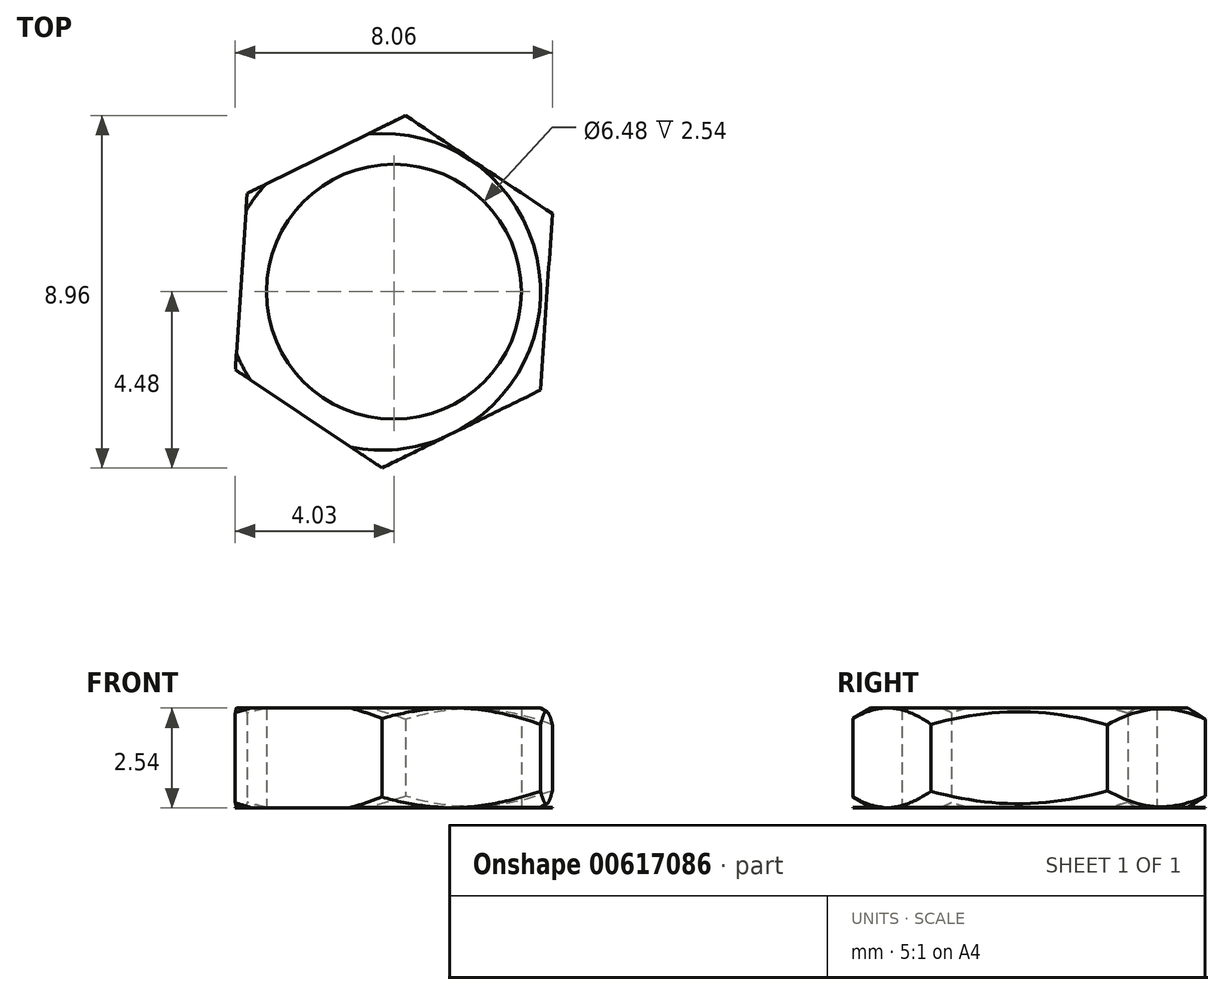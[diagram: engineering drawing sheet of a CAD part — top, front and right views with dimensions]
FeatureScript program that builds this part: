
annotation { "Feature Type Name" : "Feature", "Feature Type Description" : "" }
export const myFeature = defineFeature(function(context is Context, id is Id, definition is map)
    precondition{}
    {
        {
            var Q0;
            Q0=qCreatedBy(makeId("Top.planeOp"),FACE);
            var sketch = newSketch(context, id + "F0", { "sketchPlane" : qUnion([Q0])});
            skCircle(sketch, "E0.cCircle", {"center": v(0, 0) * mm, "radius": 3.89 * mm, "construction": true});
            skLineSegment(sketch, "E0.0", {"start": v(3.73, -2.5) * mm, "end": v(-0.3, -4.48) * mm});
            skLineSegment(sketch, "E0.1", {"start": v(-0.3, -4.48) * mm, "end": v(-4.03, -1.98) * mm});
            skLineSegment(sketch, "E0.2", {"start": v(-4.03, -1.98) * mm, "end": v(-3.73, 2.5) * mm});
            skLineSegment(sketch, "E0.3", {"start": v(-3.73, 2.5) * mm, "end": v(0.3, 4.48) * mm});
            skLineSegment(sketch, "E0.4", {"start": v(0.3, 4.48) * mm, "end": v(4.03, 1.98) * mm});
            skLineSegment(sketch, "E0.5", {"start": v(4.03, 1.98) * mm, "end": v(3.73, -2.5) * mm});
            skPoint(sketch, "E0.0.midPoint", {"position": v(1.71, -3.49) * mm});
            skCircle(sketch, "E1", {"center": v(0, 0) * mm, "radius": 3.24 * mm});
            skSolve(sketch);
        }
        {
            var Q0;
            Q0=makeQuery(id+"F0.imprint","IMPRINT",FACE,{"disambiguationData":[TD([[makeQuery(id+"F0.imprint","IMPRINT",EDGE,{"derivedFrom":sQuery(id+"F0.wireOp",EDGE,"E0.0")}),-1.0]])]});
            extrude(context, id + "F1", {"entities" : qUnion([Q0]), "depth" : 2.54 * mm, "offsetDistance" : 25.4 * mm});
        }
        {
            var Q0;
            Q0=qCreatedBy(makeId("Front.planeOp"),FACE);
            var sketch = newSketch(context, id + "F2", { "sketchPlane" : qUnion([Q0])});
            skLineSegment(sketch, "E2", {"start": v(-0.3, 0) * mm, "end": v(-0.3, 2.56) * mm, "construction": true});
            skLineSegment(sketch, "E3", {"start": v(-0.3, 2.56) * mm, "end": v(-0.3, 1.28) * mm, "construction": true});
            skLineSegment(sketch, "E4", {"start": v(-0.3, 1.28) * mm, "end": v(3.62, 1.28) * mm, "construction": true});
            skLineSegment(sketch, "E5", {"start": v(3.73, 2.54) * mm, "end": v(5.87, 2.54) * mm});
            skLineSegment(sketch, "E6", {"start": v(5.87, 2.54) * mm, "end": v(5.87, 1.3) * mm});
            skLineSegment(sketch, "E7", {"start": v(5.87, 1.3) * mm, "end": v(3.73, 2.54) * mm});
            skLineSegment(sketch, "E8.MirrorCS", {"start": v(5.87, 1.25) * mm, "end": v(3.73, 0.02) * mm});
            skLineSegment(sketch, "E9.MirrorCS", {"start": v(3.73, 0.02) * mm, "end": v(5.87, 0.02) * mm});
            skLineSegment(sketch, "E10.MirrorCS", {"start": v(5.87, 0.02) * mm, "end": v(5.87, 1.25) * mm});
            skSolve(sketch);
        }
        {
            var Q0;
            Q0 = qSketchRegion(id + "F2", true);
            var Q1;
            Q1=sQuery(id+"F2.wireOp",EDGE,"E2");
            revolve(context, id + "F3", {"operationType" : NewBodyOperationType.REMOVE, "entities" : qUnion([Q0]), "axis" : qUnion([Q1]), "revolveType" : RevolveType.FULL, "oppositeDirection" : true});
        }
    });
